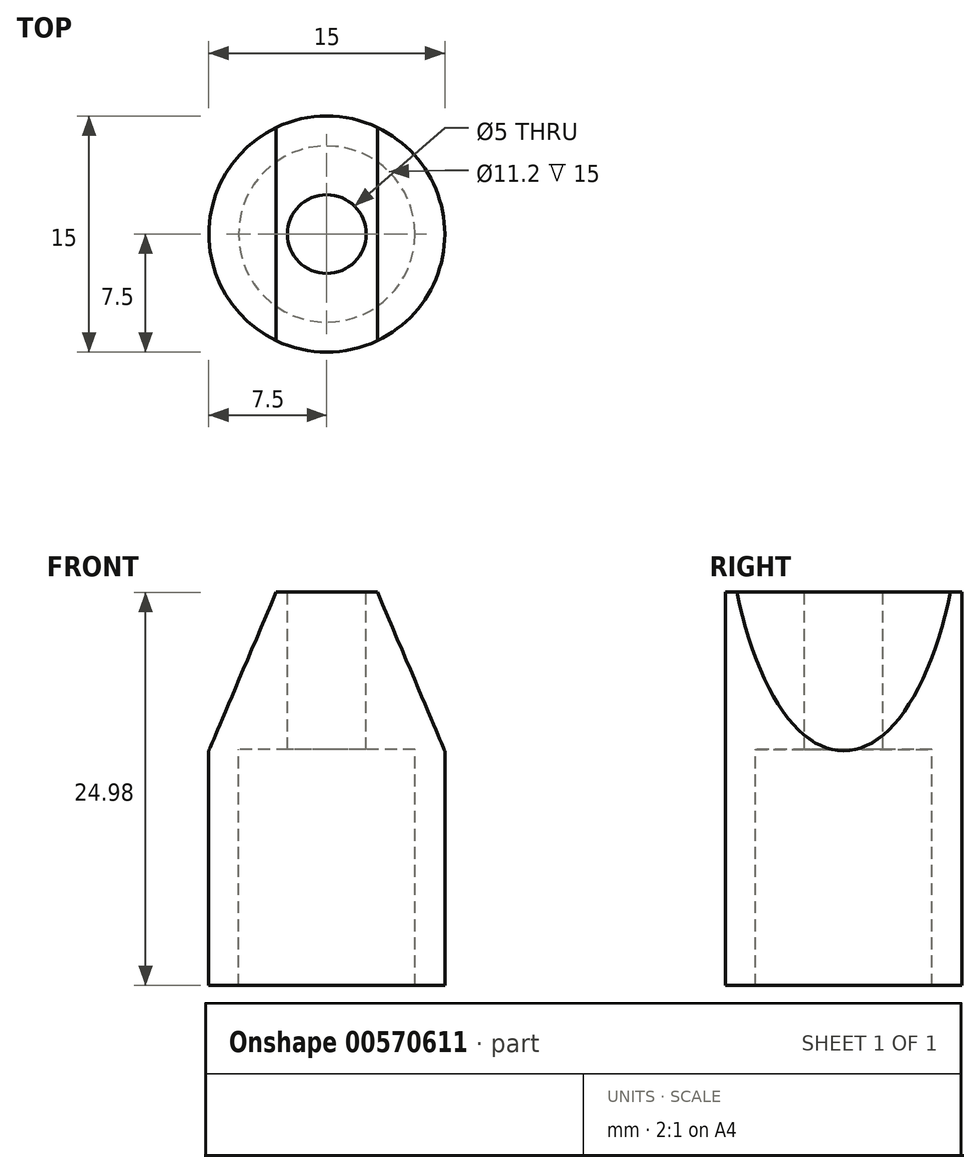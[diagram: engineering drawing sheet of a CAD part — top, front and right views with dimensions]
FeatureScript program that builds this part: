
annotation { "Feature Type Name" : "Feature", "Feature Type Description" : "" }
export const myFeature = defineFeature(function(context is Context, id is Id, definition is map)
    precondition{}
    {
        {
            var Q0;
            Q0=qCreatedBy(makeId("Front.planeOp"),FACE);
            var sketch = newSketch(context, id + "F0", { "sketchPlane" : qUnion([Q0])});
            skLineSegment(sketch, "E0", {"start": v(7.5, 0) * mm, "end": v(5.6, 0) * mm});
            skLineSegment(sketch, "E1", {"start": v(5.6, 0) * mm, "end": v(5.6, 15) * mm});
            skLineSegment(sketch, "E2", {"start": v(5.6, 15) * mm, "end": v(2.5, 15) * mm});
            skLineSegment(sketch, "E3", {"start": v(2.5, 15) * mm, "end": v(2.5, 25) * mm});
            skLineSegment(sketch, "E4", {"start": v(2.5, 25) * mm, "end": v(7.5, 25) * mm});
            skLineSegment(sketch, "E5", {"start": v(7.5, 25) * mm, "end": v(7.5, 0) * mm});
            skLineSegment(sketch, "E6", {"start": v(0, 18.43) * mm, "end": v(0, 12.6) * mm});
            skSolve(sketch);
        }
        {
            var Q0;
            Q0=makeQuery(id+"F0.imprint","IMPRINT",FACE,{"disambiguationData":[TD([[makeQuery(id+"F0.imprint","IMPRINT",EDGE,{"derivedFrom":sQuery(id+"F0.wireOp",EDGE,"E0")}),-1.0]])]});
            var Q1;
            Q1=sQuery(id+"F0.wireOp",EDGE,"E6");
            revolve(context, id + "F1", {"entities" : qUnion([Q0]), "axis" : qUnion([Q1]), "revolveType" : RevolveType.FULL});
        }
        {
            var Q0;
            Q0=qCreatedBy(makeId("Front.planeOp"),FACE);
            var sketch = newSketch(context, id + "F2", { "sketchPlane" : qUnion([Q0])});
            skLineSegment(sketch, "E7", {"start": v(-3.22, 24.98) * mm, "end": v(-10, 9) * mm});
            skLineSegment(sketch, "E8", {"start": v(-10, 9) * mm, "end": v(-10, 29) * mm});
            skLineSegment(sketch, "E9", {"start": v(-10, 29) * mm, "end": v(10, 29) * mm});
            skLineSegment(sketch, "E10", {"start": v(10, 29) * mm, "end": v(10, 9) * mm});
            skLineSegment(sketch, "E11", {"start": v(10, 9) * mm, "end": v(3.22, 24.98) * mm});
            skLineSegment(sketch, "E12", {"start": v(3.22, 24.98) * mm, "end": v(-3.22, 24.98) * mm});
            skSolve(sketch);
        }
        {
            var Q0;
            Q0=makeQuery(id+"F2.imprint","IMPRINT",FACE,{"disambiguationData":[TD([[makeQuery(id+"F2.imprint","IMPRINT",EDGE,{"derivedFrom":sQuery(id+"F2.wireOp",EDGE,"E7")}),-1.0]])]});
            extrude(context, id + "F3", {"entities" : qUnion([Q0]), "operationType" : NewBodyOperationType.REMOVE, "endBound" : BoundingType.SYMMETRIC, "oppositeDirection" : true, "depth" : 25 * mm, "offsetDistance" : 25 * mm});
        }
    });
